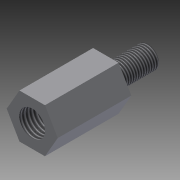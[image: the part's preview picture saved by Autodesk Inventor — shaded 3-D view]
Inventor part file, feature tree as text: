
AUTODESK INVENTOR PART (.ipt)
format: ipt  version: 2015 (Build 190159000, 159)  size: 94,720 bytes
history: native  units: mm
features: extrude x3, sketch x3, thread x2
ambient origin geometry x8: Origin, YZ Plane, XZ Plane, XY Plane, X Axis, Y Axis, Z Axis, Center Point
bodies: Solid1 (feature_tree)
feature tree (8):
  extrude  "Extrusion1"  Depth=10.0mm TaperAngle=0.0deg
  sketch  "Sketch2"  dims[d4=3.5mm d5=3.0mm]
  extrude  "Extrusion2"  Depth=3.0mm
  extrude  "Extrusion3"  Depth=6.0mm TaperAngle=0.0deg
  thread  "Thread1"  [1 undecoded]
  thread  "Thread2"  [1 undecoded]
  sketch  "Sketch1"  dims[d1=6.0mm d2=10.0mm d3=0.0mm]
  sketch  "Sketch3"  dims[d6=5.7mm d7=0.0mm d8=6.0mm d9=0.0mm d10=10.0mm d11=0.0mm d12=10.0mm d13=0.0mm]
note: 2 required parameter values undecoded (feature->parameter linkage not recoverable at this tier; creation-order binding heuristic only, values carry confidence <= 0.55)
